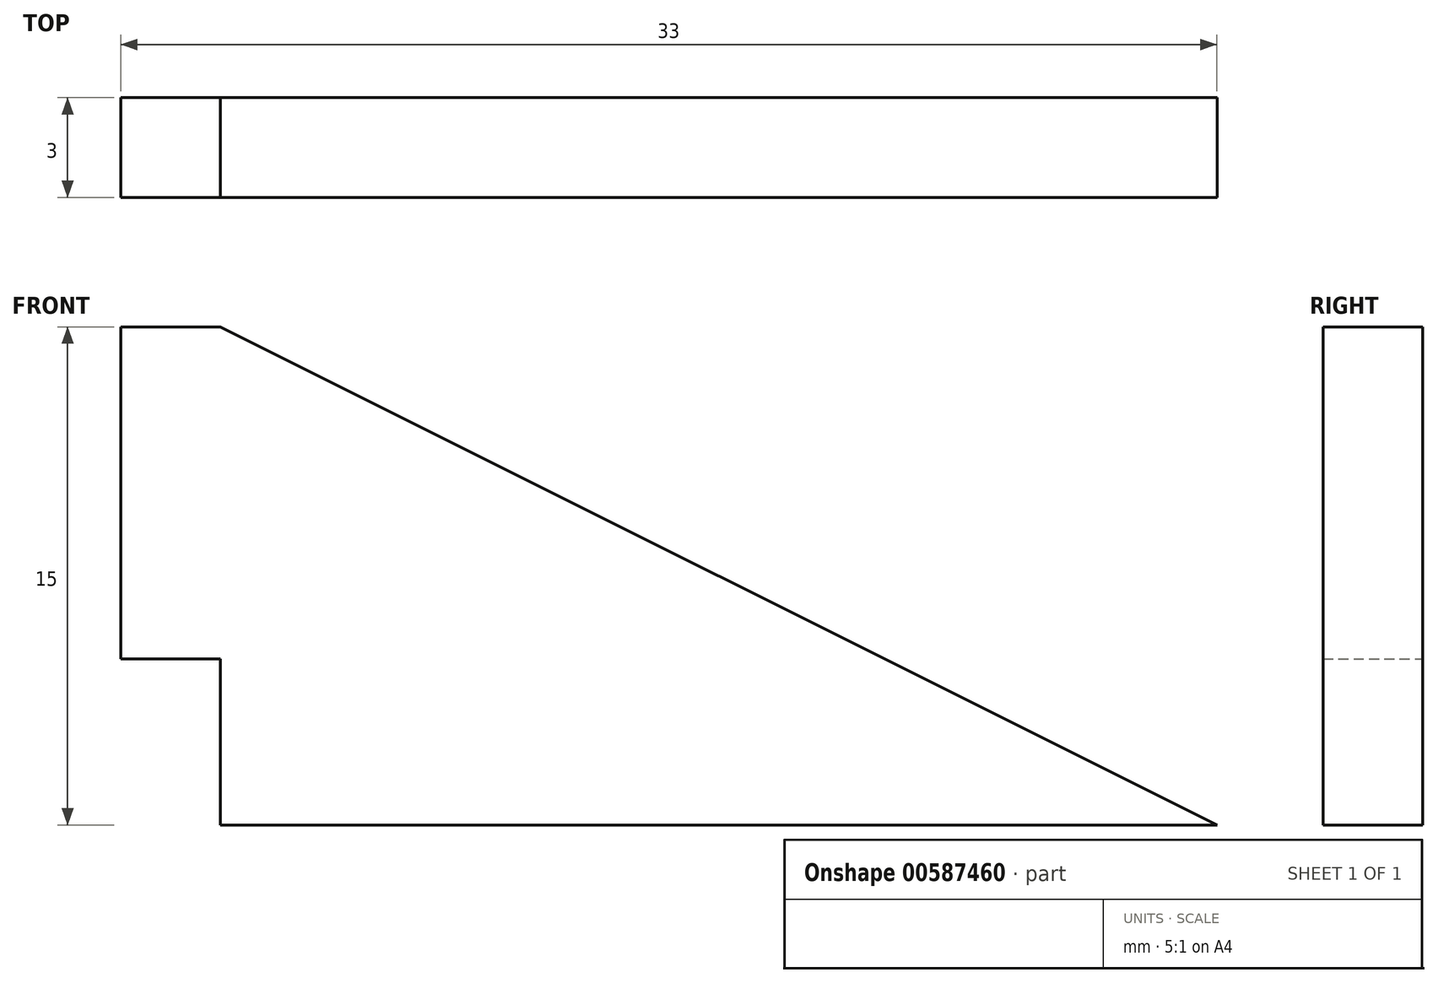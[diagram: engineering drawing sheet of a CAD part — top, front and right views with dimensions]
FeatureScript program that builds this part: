
annotation { "Feature Type Name" : "Feature", "Feature Type Description" : "" }
export const myFeature = defineFeature(function(context is Context, id is Id, definition is map)
    precondition{}
    {
        {
            var Q0;
            Q0=qCreatedBy(makeId("Front.planeOp"),FACE);
            var sketch = newSketch(context, id + "F0", { "sketchPlane" : qUnion([Q0])});
            skLineSegment(sketch, "E0", {"start": v(-46.88, -1.53) * mm, "end": v(-46.88, -16.53) * mm});
            skLineSegment(sketch, "E1", {"start": v(-46.88, -16.53) * mm, "end": v(-16.88, -16.53) * mm});
            skLineSegment(sketch, "E2", {"start": v(-16.88, -16.53) * mm, "end": v(-46.88, -1.53) * mm});
            skLineSegment(sketch, "E3", {"start": v(-46.88, -1.53) * mm, "end": v(-49.88, -1.53) * mm});
            skLineSegment(sketch, "E4", {"start": v(-49.88, -1.53) * mm, "end": v(-49.88, -11.53) * mm});
            skLineSegment(sketch, "E5", {"start": v(-49.88, -11.53) * mm, "end": v(-46.88, -11.53) * mm});
            skSolve(sketch);
        }
        {
            var Q0;
            Q0 = qSketchRegion(id + "F0", true);
            extrude(context, id + "F1", {"entities" : qUnion([Q0]), "depth" : 3 * mm, "offsetDistance" : 25 * mm});
        }
    });
